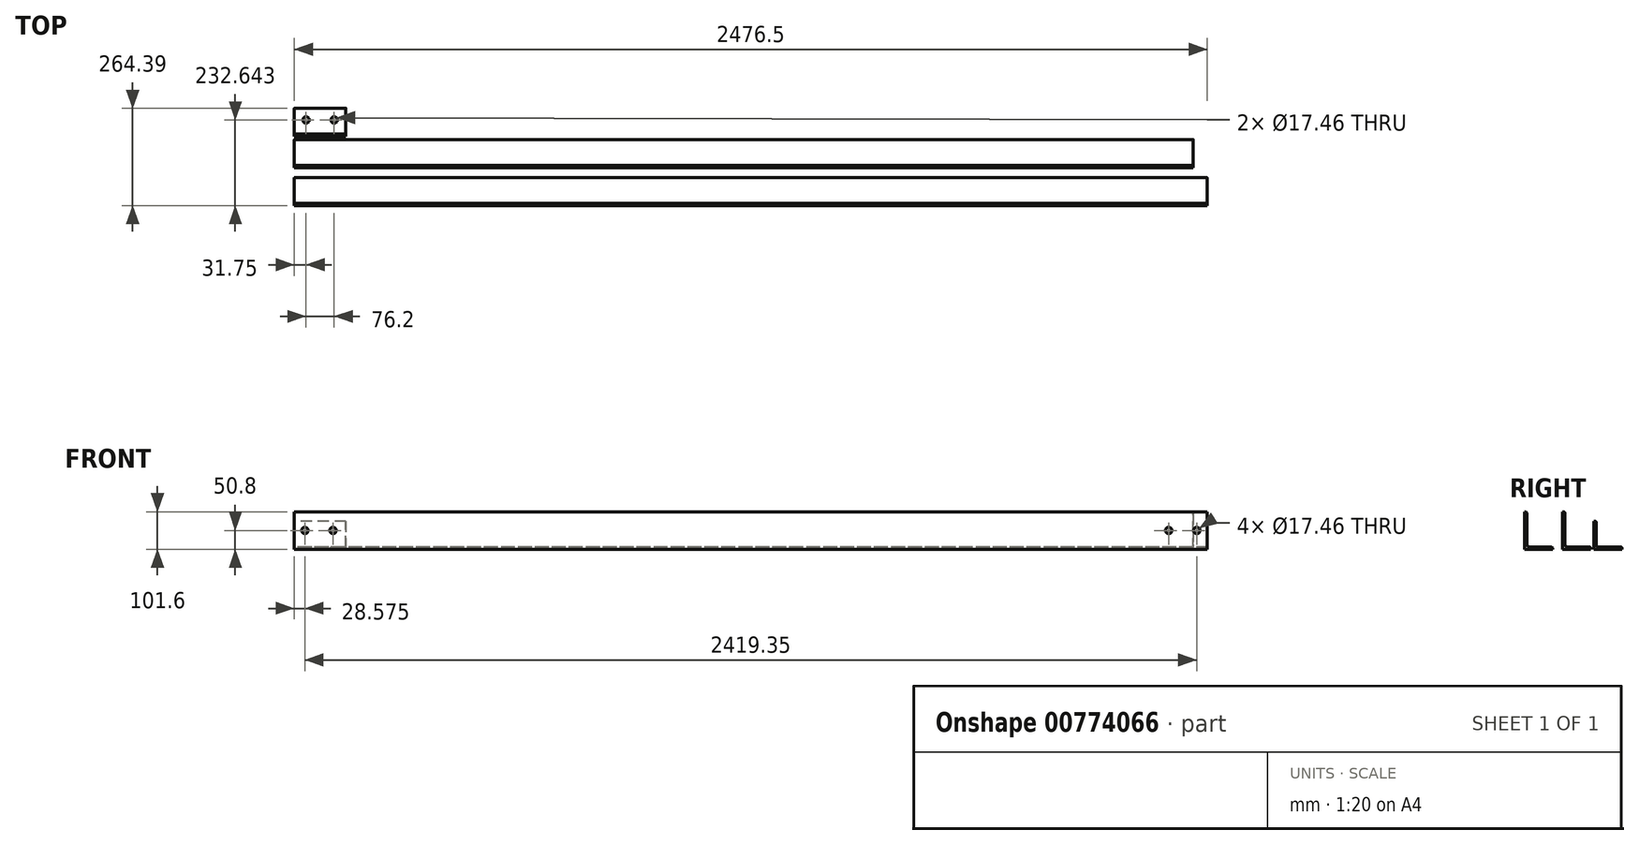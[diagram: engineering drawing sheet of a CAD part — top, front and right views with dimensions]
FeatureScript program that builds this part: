
annotation { "Feature Type Name" : "Feature", "Feature Type Description" : "" }
export const myFeature = defineFeature(function(context is Context, id is Id, definition is map)
    precondition{}
    {
        {
            var Q0;
            Q0=qCreatedBy(makeId("Right.planeOp"),FACE);
            var sketch = newSketch(context, id + "F0", { "sketchPlane" : qUnion([Q0])});
            skLineSegment(sketch, "E0", {"start": v(0, 0) * mm, "end": v(0, 101.6) * mm});
            skLineSegment(sketch, "E1", {"start": v(0, 0) * mm, "end": v(76.2, 0) * mm});
            skLineSegment(sketch, "E2", {"start": v(0, 101.6) * mm, "end": v(1.27, 101.6) * mm});
            skLineSegment(sketch, "E3", {"start": v(6.35, 96.52) * mm, "end": v(6.35, 12.7) * mm});
            skLineSegment(sketch, "E4", {"start": v(12.7, 6.35) * mm, "end": v(71.12, 6.35) * mm});
            skLineSegment(sketch, "E5", {"start": v(76.2, 1.27) * mm, "end": v(76.2, 0) * mm});
            skPoint(sketch, "E6.visualSharp", {"position": v(6.35, 6.35) * mm});
            skArc(sketch, "E6.filletArc", {"start": v(6.35, 12.7) * mm, "mid": v(8.2, 8.2) * mm, "end": v(12.7, 6.35) * mm});
            skPoint(sketch, "E7.visualSharp", {"position": v(6.35, 101.6) * mm});
            skArc(sketch, "E7.filletArc", {"start": v(6.35, 96.52) * mm, "mid": v(4.86, 100.11) * mm, "end": v(1.27, 101.6) * mm});
            skPoint(sketch, "E8.visualSharp", {"position": v(76.2, 6.35) * mm});
            skArc(sketch, "E8.filletArc", {"start": v(76.2, 1.27) * mm, "mid": v(74.71, 4.86) * mm, "end": v(71.12, 6.35) * mm});
            skSolve(sketch);
        }
        {
            var Q0;
            Q0=makeQuery(id+"F0.imprint","IMPRINT",FACE,{"disambiguationData":[TD([[makeQuery(id+"F0.imprint","IMPRINT",EDGE,{"derivedFrom":sQuery(id+"F0.wireOp",EDGE,"E0")}),-1.0]])]});
            extrude(context, id + "F1", {"entities" : qUnion([Q0]), "depth" : 2438.4 * mm, "offsetDistance" : 25.4 * mm});
        }
        {
            var Q0;
            Q0=qCreatedBy(makeId("Right.planeOp"),FACE);
            var sketch = newSketch(context, id + "F2", { "sketchPlane" : qUnion([Q0])});
            skArc(sketch, "E9.0.0", {"start": v(-96.87, 12.7) * mm, "mid": v(-95, 8.2) * mm, "end": v(-90.52, 6.35) * mm});
            skLineSegment(sketch, "E9.0.1", {"start": v(-90.52, 6.35) * mm, "end": v(-32.1, 6.35) * mm});
            skArc(sketch, "E9.0.2", {"start": v(-32.1, 6.35) * mm, "mid": v(-28.5, 4.86) * mm, "end": v(-27.02, 1.27) * mm});
            skLineSegment(sketch, "E9.0.3", {"start": v(-27.02, 1.27) * mm, "end": v(-27.02, 0) * mm});
            skLineSegment(sketch, "E9.0.4", {"start": v(-27.02, 0) * mm, "end": v(-103.22, 0) * mm});
            skLineSegment(sketch, "E9.0.5", {"start": v(-103.22, 0) * mm, "end": v(-103.22, 101.6) * mm});
            skLineSegment(sketch, "E9.0.6", {"start": v(-103.22, 101.6) * mm, "end": v(-101.95, 101.6) * mm});
            skArc(sketch, "E9.0.7", {"start": v(-101.95, 101.6) * mm, "mid": v(-98.35, 100.11) * mm, "end": v(-96.87, 96.52) * mm});
            skLineSegment(sketch, "E9.0.8", {"start": v(-96.87, 96.52) * mm, "end": v(-96.87, 12.7) * mm});
            skSolve(sketch);
        }
        {
            var Q0;
            Q0=makeQuery(id+"F2.imprint","IMPRINT",FACE,{"disambiguationData":[TD([[makeQuery(id+"F2.imprint","IMPRINT",EDGE,{"derivedFrom":sQuery(id+"F2.wireOp",EDGE,"E9.0.0")}),-1.0]])]});
            extrude(context, id + "F3", {"entities" : qUnion([Q0]), "depth" : 2476.5 * mm, "offsetDistance" : 25.4 * mm});
        }
        {
            var Q0;
            Q0=qCreatedBy(makeId("Right.planeOp"),FACE);
            var sketch = newSketch(context, id + "F4", { "sketchPlane" : qUnion([Q0])});
            skLineSegment(sketch, "E10", {"start": v(84.97, 76.2) * mm, "end": v(84.97, 0) * mm});
            skLineSegment(sketch, "E11", {"start": v(84.97, 0) * mm, "end": v(161.17, 0) * mm});
            skLineSegment(sketch, "E12", {"start": v(161.17, 0) * mm, "end": v(161.17, 6.35) * mm});
            skLineSegment(sketch, "E13", {"start": v(161.17, 6.35) * mm, "end": v(91.32, 6.35) * mm});
            skLineSegment(sketch, "E14", {"start": v(91.32, 6.35) * mm, "end": v(91.32, 76.2) * mm});
            skLineSegment(sketch, "E15", {"start": v(84.97, 76.2) * mm, "end": v(91.32, 76.2) * mm});
            skSolve(sketch);
        }
        {
            var Q0;
            Q0=makeQuery(id+"F4.imprint","IMPRINT",FACE,{"disambiguationData":[TD([[makeQuery(id+"F4.imprint","IMPRINT",EDGE,{"derivedFrom":sQuery(id+"F4.wireOp",EDGE,"E10")}),1.0]])]});
            extrude(context, id + "F5", {"entities" : qUnion([Q0]), "depth" : 139.7 * mm, "offsetDistance" : 25.4 * mm});
        }
        {
            var Q0;
            Q0=makeQuery(id+"F5.opExtrude","SWEPT_EDGE",EDGE,{"disambiguationData":[OSD([sQuery(id+"F4.wireOp",EDGE,"E14"),sQuery(id+"F4.wireOp",EDGE,"E15")])]});
            var Q1;
            Q1=makeQuery(id+"F5.opExtrude","SWEPT_EDGE",EDGE,{"disambiguationData":[OSD([sQuery(id+"F4.wireOp",EDGE,"E12"),sQuery(id+"F4.wireOp",EDGE,"E13")])]});
            fillet(context, id + "F6", {"entities" : qUnion([Q0, Q1]), "radius" : 5.08 * mm, "tangentPropagation" : true, "allowEdgeOverflow" : false});
        }
        {
            var Q0;
            Q0=makeQuery(id+"F5.opExtrude","SWEPT_FACE",FACE,{"disambiguationData":[OSD([sQuery(id+"F4.wireOp",EDGE,"E13")])]});
            var sketch = newSketch(context, id + "F7", { "sketchPlane" : qUnion([Q0])});
            skCircle(sketch, "E16", {"center": v(31.75, 129.42) * mm, "radius": 8.73 * mm});
            skCircle(sketch, "E17", {"center": v(107.95, 129.42) * mm, "radius": 8.73 * mm});
            skSolve(sketch);
        }
        {
            var Q0;
            Q0 = qSketchRegion(id + "F7", true);
            extrude(context, id + "F8", {"entities" : qUnion([Q0]), "operationType" : NewBodyOperationType.REMOVE, "endBound" : BoundingType.THROUGH_ALL, "oppositeDirection" : true, "depth" : 25.4 * mm, "offsetDistance" : 25.4 * mm});
        }
        {
            var Q0;
            Q0=makeQuery(id+"F3.opExtrude","SWEPT_FACE",FACE,{"disambiguationData":[OSD([sQuery(id+"F2.wireOp",EDGE,"E9.0.5")])]});
            var sketch = newSketch(context, id + "F9", { "sketchPlane" : qUnion([Q0])});
            skCircle(sketch, "E18", {"center": v(28.58, 50.8) * mm, "radius": 8.73 * mm});
            skPoint(sketch, "E18.centerSnap0", {"position": v(0, 50.8) * mm});
            skCircle(sketch, "E19", {"center": v(104.78, 50.8) * mm, "radius": 8.73 * mm});
            skLineSegment(sketch, "E20", {"start": v(1238.25, 101.6) * mm, "end": v(1238.25, 0) * mm, "construction": true});
            skCircle(sketch, "E21.MirrorC", {"center": v(2447.93, 50.8) * mm, "radius": 8.73 * mm});
            skCircle(sketch, "E22.MirrorC", {"center": v(2371.72, 50.8) * mm, "radius": 8.73 * mm});
            skPoint(sketch, "E23.MirrorP", {"position": v(2476.5, 50.8) * mm});
            skSolve(sketch);
        }
        {
            var Q0;
            Q0 = qSketchRegion(id + "F9", true);
            extrude(context, id + "F10", {"entities" : qUnion([Q0]), "operationType" : NewBodyOperationType.REMOVE, "oppositeDirection" : true, "depth" : 25.4 * mm, "offsetDistance" : 25.4 * mm});
        }
    });
